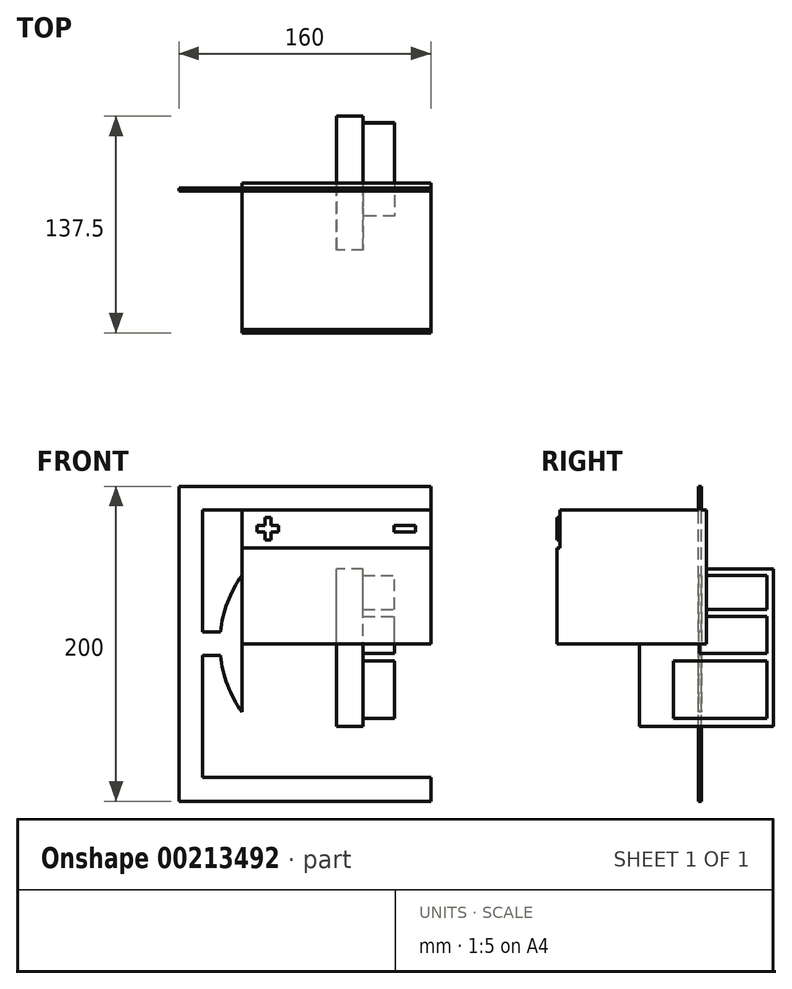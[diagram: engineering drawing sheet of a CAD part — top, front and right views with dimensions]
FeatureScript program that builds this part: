
annotation { "Feature Type Name" : "Feature", "Feature Type Description" : "" }
export const myFeature = defineFeature(function(context is Context, id is Id, definition is map)
    precondition{}
    {
        {
            var Q0;
            Q0=qCreatedBy(makeId("Front.planeOp"),FACE);
            var sketch = newSketch(context, id + "F0", { "sketchPlane" : qUnion([Q0])});
            skCircle(sketch, "E0", {"center": v(0, 0) * mm, "radius": 10 * mm});
            skSolve(sketch);
        }
        {
            var Q0;
            Q0 = qSketchRegion(id + "F0", true);
            extrude(context, id + "F1", {"entities" : qUnion([Q0]), "depth" : 3 * mm});
        }
        {
            var Q0;
            Q0=makeQuery(id+"F1.opExtrude","CAP_FACE",FACE,{"disambiguationData":[OSD([sQuery(id+"F0.wireOp",EDGE,"E0")])],"isStart":false});
            var sketch = newSketch(context, id + "F2", { "sketchPlane" : qUnion([Q0])});
            skCircle(sketch, "E1", {"center": v(0, 0) * mm, "radius": 15 * mm});
            skSolve(sketch);
        }
        {
            var Q0;
            Q0 = qSketchRegion(id + "F2", true);
            extrude(context, id + "F3", {"entities" : qUnion([Q0]), "operationType" : NewBodyOperationType.ADD, "depth" : 1 * mm});
        }
        {
            var Q0;
            Q0=makeQuery(id+"F3.opExtrude","CAP_FACE",FACE,{"disambiguationData":[OSD([sQuery(id+"F2.wireOp",EDGE,"E1")])],"isStart":false});
            var sketch = newSketch(context, id + "F4", { "sketchPlane" : qUnion([Q0])});
            skCircle(sketch, "E2", {"center": v(0, 0) * mm, "radius": 6 * mm});
            skSolve(sketch);
        }
        {
            var Q0;
            Q0 = qSketchRegion(id + "F4", true);
            extrude(context, id + "F5", {"entities" : qUnion([Q0]), "operationType" : NewBodyOperationType.REMOVE, "endBound" : BoundingType.THROUGH_ALL, "oppositeDirection" : true, "depth" : 25 * mm});
        }
        {
            var Q0;
            Q0=makeQuery(id+"F3.opExtrude","CAP_FACE",FACE,{"disambiguationData":[OSD([sQuery(id+"F2.wireOp",EDGE,"E1")])],"isStart":false});
            var sketch = newSketch(context, id + "F6", { "sketchPlane" : qUnion([Q0])});
            skCircle(sketch, "E3", {"center": v(0, 0) * mm, "radius": 15 * mm});
            skCircle(sketch, "E4", {"center": v(0, 0) * mm, "radius": 4.75 * mm});
            skSolve(sketch);
        }
        {
            var Q0;
            Q0 = qSketchRegion(id + "F6", true);
            extrude(context, id + "F7", {"entities" : qUnion([Q0]), "operationType" : NewBodyOperationType.ADD, "depth" : 1 * mm});
        }
        {
            var Q0;
            Q0=makeQuery(id+"F1.opExtrude","CAP_EDGE",EDGE,{"disambiguationData":[OSD([sQuery(id+"F0.wireOp",EDGE,"E0")])],"isStart":true});
            chamfer(context, id + "F8", {"entities" : qUnion([Q0]), "width" : 1 * mm, "tangentPropagation" : true});
        }
        {
            var Q0;
            Q0=makeQuery(id+"F7.opExtrude","CAP_FACE",FACE,{"disambiguationData":[OSD([sQuery(id+"F6.wireOp",EDGE,"E3"),sQuery(id+"F6.wireOp",EDGE,"E4")])],"isStart":false});
            var sketch = newSketch(context, id + "F9", { "sketchPlane" : qUnion([Q0])});
            skLineSegment(sketch, "E5.bottom", {"start": v(-7.5, 100) * mm, "end": v(7.5, 100) * mm});
            skLineSegment(sketch, "E5.top", {"start": v(-7.5, -100) * mm, "end": v(7.5, -100) * mm});
            skLineSegment(sketch, "E5.left", {"start": v(-7.5, 85) * mm, "end": v(-7.5, 7.5) * mm});
            skLineSegment(sketch, "E5.right", {"start": v(7.5, 85) * mm, "end": v(7.5, 7.5) * mm});
            skPoint(sketch, "E5.middle", {"position": v(0, 0) * mm});
            skLineSegment(sketch, "E6.bottom", {"start": v(-85, 7.5) * mm, "end": v(-7.5, 7.5) * mm});
            skLineSegment(sketch, "E6.top", {"start": v(-85, -7.5) * mm, "end": v(-7.5, -7.5) * mm});
            skPoint(sketch, "E6.middle", {"position": v(-16.68, 0) * mm});
            skCircle(sketch, "E7", {"center": v(0, 0) * mm, "radius": 6.5 * mm});
            skLineSegment(sketch, "E8.trimOffspring", {"start": v(7.5, -7.5) * mm, "end": v(45, -7.5) * mm});
            skLineSegment(sketch, "E9.trimOffspring", {"start": v(7.5, -7.5) * mm, "end": v(7.5, -85) * mm});
            skLineSegment(sketch, "E10.trimOffspring", {"start": v(7.5, 7.5) * mm, "end": v(45, 7.5) * mm});
            skLineSegment(sketch, "E11.trimOffspring", {"start": v(-7.5, -7.5) * mm, "end": v(-7.5, -85) * mm});
            skLineSegment(sketch, "E12.bottom", {"start": v(-100, -100) * mm, "end": v(-7.5, -100) * mm});
            skLineSegment(sketch, "E12.top", {"start": v(-100, 100) * mm, "end": v(-7.5, 100) * mm});
            skLineSegment(sketch, "E12.left", {"start": v(-100, -100) * mm, "end": v(-100, 100) * mm});
            skLineSegment(sketch, "E12.right", {"start": v(60, -100) * mm, "end": v(60, 100) * mm});
            skLineSegment(sketch, "E13.0", {"start": v(45, -85) * mm, "end": v(45, -7.5) * mm});
            skLineSegment(sketch, "E13.1", {"start": v(-85, -85) * mm, "end": v(-7.5, -85) * mm});
            skLineSegment(sketch, "E13.2", {"start": v(-85, -85) * mm, "end": v(-85, -7.5) * mm});
            skLineSegment(sketch, "E13.3", {"start": v(-85, 85) * mm, "end": v(-7.5, 85) * mm});
            skLineSegment(sketch, "E14.trimOffspring", {"start": v(45, 7.5) * mm, "end": v(45, 85) * mm});
            skLineSegment(sketch, "E15.trimOffspring", {"start": v(7.5, 85) * mm, "end": v(45, 85) * mm});
            skLineSegment(sketch, "E16.trimOffspring", {"start": v(7.5, -85) * mm, "end": v(45, -85) * mm});
            skLineSegment(sketch, "E17.trimOffspring", {"start": v(-85, 7.5) * mm, "end": v(-85, 85) * mm});
            skLineSegment(sketch, "E18.trimOffspring", {"start": v(7.5, -100) * mm, "end": v(60, -100) * mm});
            skLineSegment(sketch, "E19.trimOffspring", {"start": v(7.5, 100) * mm, "end": v(60, 100) * mm});
            skSolve(sketch);
        }
        {
            var Q0;
            Q0 = qSketchRegion(id + "F9", true);
            extrude(context, id + "F10", {"entities" : qUnion([Q0]), "operationType" : NewBodyOperationType.ADD, "oppositeDirection" : true, "depth" : 2 * mm});
        }
        {
            var Q0;
            Q0=makeQuery(id+"F10.boolean.opBoolean","MERGE",FACE,{"derivedFrom":[makeQuery(id+"F7.opExtrude","CAP_FACE",FACE,{"disambiguationData":[OSD([sQuery(id+"F6.wireOp",EDGE,"E3"),sQuery(id+"F6.wireOp",EDGE,"E4")])],"isStart":false}),makeQuery(id+"F10.opExtrude","CAP_FACE",FACE,{"disambiguationData":[OSD([sQuery(id+"F9.wireOp",EDGE,"E5.bottom"),sQuery(id+"F9.wireOp",EDGE,"E5.top"),sQuery(id+"F9.wireOp",EDGE,"E5.left"),sQuery(id+"F9.wireOp",EDGE,"E5.right"),sQuery(id+"F9.wireOp",EDGE,"E6.bottom"),sQuery(id+"F9.wireOp",EDGE,"E6.top"),sQuery(id+"F9.wireOp",EDGE,"E7"),sQuery(id+"F9.wireOp",EDGE,"E8.trimOffspring"),sQuery(id+"F9.wireOp",EDGE,"E9.trimOffspring"),sQuery(id+"F9.wireOp",EDGE,"E10.trimOffspring"),sQuery(id+"F9.wireOp",EDGE,"E11.trimOffspring"),sQuery(id+"F9.wireOp",EDGE,"E12.bottom"),sQuery(id+"F9.wireOp",EDGE,"E12.top"),sQuery(id+"F9.wireOp",EDGE,"E12.left"),sQuery(id+"F9.wireOp",EDGE,"E12.right"),sQuery(id+"F9.wireOp",EDGE,"E13.0"),sQuery(id+"F9.wireOp",EDGE,"E13.1"),sQuery(id+"F9.wireOp",EDGE,"E13.2"),sQuery(id+"F9.wireOp",EDGE,"E13.3"),sQuery(id+"F9.wireOp",EDGE,"E14.trimOffspring"),sQuery(id+"F9.wireOp",EDGE,"E15.trimOffspring"),sQuery(id+"F9.wireOp",EDGE,"E16.trimOffspring"),sQuery(id+"F9.wireOp",EDGE,"E17.trimOffspring"),sQuery(id+"F9.wireOp",EDGE,"E18.trimOffspring"),sQuery(id+"F9.wireOp",EDGE,"E19.trimOffspring")])],"isStart":true})]});
            var sketch = newSketch(context, id + "F11", { "sketchPlane" : qUnion([Q0])});
            skCircle(sketch, "E20", {"center": v(0, 0) * mm, "radius": 55 * mm});
            skArc(sketch, "E21", {"start": v(60, 43.31) * mm, "mid": v(-74, 0) * mm, "end": v(60, -43.31) * mm});
            skLineSegment(sketch, "E22", {"start": v(60, 43.31) * mm, "end": v(60, -43.31) * mm});
            skSolve(sketch);
        }
        {
            var Q0;
            Q0 = qSketchRegion(id + "F11", true);
            extrude(context, id + "F12", {"entities" : qUnion([Q0]), "operationType" : NewBodyOperationType.ADD, "oppositeDirection" : true, "depth" : 2 * mm});
        }
        {
            var Q0;
            Q0=makeQuery(id+"F12.boolean.opBoolean","MERGE",FACE,{"derivedFrom":[makeQuery(id+"F10.boolean.opBoolean","MERGE",FACE,{"derivedFrom":[makeQuery(id+"F7.opExtrude","CAP_FACE",FACE,{"disambiguationData":[OSD([sQuery(id+"F6.wireOp",EDGE,"E3"),sQuery(id+"F6.wireOp",EDGE,"E4")])],"isStart":false}),makeQuery(id+"F10.opExtrude","CAP_FACE",FACE,{"disambiguationData":[OSD([sQuery(id+"F9.wireOp",EDGE,"E5.bottom"),sQuery(id+"F9.wireOp",EDGE,"E5.top"),sQuery(id+"F9.wireOp",EDGE,"E5.left"),sQuery(id+"F9.wireOp",EDGE,"E5.right"),sQuery(id+"F9.wireOp",EDGE,"E6.bottom"),sQuery(id+"F9.wireOp",EDGE,"E6.top"),sQuery(id+"F9.wireOp",EDGE,"E7"),sQuery(id+"F9.wireOp",EDGE,"E8.trimOffspring"),sQuery(id+"F9.wireOp",EDGE,"E9.trimOffspring"),sQuery(id+"F9.wireOp",EDGE,"E10.trimOffspring"),sQuery(id+"F9.wireOp",EDGE,"E11.trimOffspring"),sQuery(id+"F9.wireOp",EDGE,"E12.bottom"),sQuery(id+"F9.wireOp",EDGE,"E12.top"),sQuery(id+"F9.wireOp",EDGE,"E12.left"),sQuery(id+"F9.wireOp",EDGE,"E12.right"),sQuery(id+"F9.wireOp",EDGE,"E13.0"),sQuery(id+"F9.wireOp",EDGE,"E13.1"),sQuery(id+"F9.wireOp",EDGE,"E13.2"),sQuery(id+"F9.wireOp",EDGE,"E13.3"),sQuery(id+"F9.wireOp",EDGE,"E14.trimOffspring"),sQuery(id+"F9.wireOp",EDGE,"E15.trimOffspring"),sQuery(id+"F9.wireOp",EDGE,"E16.trimOffspring"),sQuery(id+"F9.wireOp",EDGE,"E17.trimOffspring"),sQuery(id+"F9.wireOp",EDGE,"E18.trimOffspring"),sQuery(id+"F9.wireOp",EDGE,"E19.trimOffspring")])],"isStart":true})]}),makeQuery(id+"F12.opExtrude","CAP_FACE",FACE,{"disambiguationData":[OSD([sQuery(id+"F11.wireOp",EDGE,"E20"),sQuery(id+"F11.wireOp",EDGE,"E21"),sQuery(id+"F11.wireOp",EDGE,"E22")])],"isStart":true})]});
            var sketch = newSketch(context, id + "F13", { "sketchPlane" : qUnion([Q0])});
            skLineSegment(sketch, "E23", {"start": v(0, 0) * mm, "end": v(32.2, -50.62) * mm, "construction": true});
            skLineSegment(sketch, "E24", {"start": v(32.2, -50.62) * mm, "end": v(13.65, -62.43) * mm, "construction": true});
            skPoint(sketch, "E25.MirrorP", {"position": v(50.77, -38.81) * mm});
            skCircle(sketch, "E26", {"center": v(0, 0) * mm, "radius": 36.29 * mm, "construction": true});
            skPoint(sketch, "E27.1.0", {"position": v(-47.84, -52.18) * mm});
            skPoint(sketch, "E27.1.1", {"position": v(-9.28, -73.36) * mm});
            skPoint(sketch, "E27.2.0", {"position": v(-68.43, 6.67) * mm});
            skPoint(sketch, "E27.2.1", {"position": v(-68.46, -37.33) * mm});
            skPoint(sketch, "E27.3.0", {"position": v(-26.74, 53.02) * mm});
            skPoint(sketch, "E27.3.1", {"position": v(-65.33, 31.88) * mm});
            skPoint(sketch, "E27.4.0", {"position": v(33.95, 38.76) * mm});
            skPoint(sketch, "E27.4.1", {"position": v(-3.15, 62.43) * mm});
            skPoint(sketch, "E27.center", {"position": v(-8.44, -5.37) * mm});
            skLineSegment(sketch, "E27.anchor1", {"start": v(-8.44, -5.37) * mm, "end": v(13.65, -62.43) * mm, "construction": true});
            skLineSegment(sketch, "E27.anchor2", {"start": v(-8.44, -5.37) * mm, "end": v(33.95, 38.76) * mm, "construction": true});
            skCircle(sketch, "E28", {"center": v(13.65, -62.43) * mm, "radius": 3.18 * mm});
            skCircle(sketch, "E29.MirrorC", {"center": v(50.77, -38.81) * mm, "radius": 3.18 * mm});
            skSolve(sketch);
        }
        {
            var Q0;
            Q0 = qSketchRegion(id + "F13", true);
            extrude(context, id + "F14", {"entities" : qUnion([Q0]), "operationType" : NewBodyOperationType.ADD, "depth" : 8 * mm});
        }
        {
            var Q0;
            Q0=qCreatedBy(makeId("Front.planeOp"),FACE);
            var sketch = newSketch(context, id + "F15", { "sketchPlane" : qUnion([Q0])});
            skLineSegment(sketch, "E30.bottom", {"start": v(60, -85) * mm, "end": v(-60, -85) * mm});
            skLineSegment(sketch, "E30.top", {"start": v(60, 85) * mm, "end": v(-60, 85) * mm});
            skLineSegment(sketch, "E30.left", {"start": v(60, -85) * mm, "end": v(60, 85) * mm});
            skLineSegment(sketch, "E30.right", {"start": v(-60, -85) * mm, "end": v(-60, 85) * mm});
            skPoint(sketch, "E30.middle", {"position": v(0, 0) * mm});
            skSolve(sketch);
        }
        {
            var Q0;
            Q0 = qSketchRegion(id + "F15", true);
            extrude(context, id + "F16", {"entities" : qUnion([Q0]), "depth" : 95 * mm});
        }
        {
            var Q0;
            Q0=makeQuery(id+"F16.opExtrude","CAP_FACE",FACE,{"disambiguationData":[OSD([sQuery(id+"F15.wireOp",EDGE,"E30.bottom"),sQuery(id+"F15.wireOp",EDGE,"E30.top"),sQuery(id+"F15.wireOp",EDGE,"E30.left"),sQuery(id+"F15.wireOp",EDGE,"E30.right")])],"isStart":false});
            var sketch = newSketch(context, id + "F17", { "sketchPlane" : qUnion([Q0])});
            skLineSegment(sketch, "E31.bottom", {"start": v(-60, 85) * mm, "end": v(60, 85) * mm});
            skLineSegment(sketch, "E31.top", {"start": v(-60, 60.98) * mm, "end": v(60, 60.98) * mm});
            skLineSegment(sketch, "E31.left", {"start": v(-60, 85) * mm, "end": v(-60, 60.98) * mm});
            skLineSegment(sketch, "E31.right", {"start": v(60, 85) * mm, "end": v(60, 60.98) * mm});
            skLineSegment(sketch, "E32.bottom", {"start": v(-50.27, 75) * mm, "end": v(-45.38, 75) * mm});
            skLineSegment(sketch, "E32.top", {"start": v(-50.27, 71.06) * mm, "end": v(-45.38, 71.06) * mm});
            skLineSegment(sketch, "E32.left", {"start": v(-50.27, 75) * mm, "end": v(-50.27, 71.06) * mm});
            skLineSegment(sketch, "E32.right", {"start": v(-36.73, 75) * mm, "end": v(-36.73, 71.06) * mm});
            skLineSegment(sketch, "E33", {"start": v(0, 71.7) * mm, "end": v(0, 43.69) * mm, "construction": true});
            skLineSegment(sketch, "E34.MirrorCS", {"start": v(50.27, 75) * mm, "end": v(36.73, 75) * mm});
            skLineSegment(sketch, "E35.MirrorCS", {"start": v(50.27, 71.06) * mm, "end": v(36.73, 71.06) * mm});
            skLineSegment(sketch, "E36.MirrorCS", {"start": v(50.27, 75) * mm, "end": v(50.27, 71.06) * mm});
            skLineSegment(sketch, "E37.MirrorCS", {"start": v(36.73, 75) * mm, "end": v(36.73, 71.06) * mm});
            skLineSegment(sketch, "E38.bottom", {"start": v(-41.62, 65.91) * mm, "end": v(-45.38, 65.91) * mm});
            skLineSegment(sketch, "E38.top", {"start": v(-41.62, 80.16) * mm, "end": v(-45.38, 80.16) * mm});
            skLineSegment(sketch, "E38.left", {"start": v(-41.62, 65.91) * mm, "end": v(-41.62, 71.06) * mm});
            skLineSegment(sketch, "E38.right", {"start": v(-45.38, 65.91) * mm, "end": v(-45.38, 71.06) * mm});
            skPoint(sketch, "E38.middle", {"position": v(-43.5, 73.03) * mm});
            skPoint(sketch, "E38.middle.positionSnap0", {"position": v(-43.5, 75) * mm});
            skPoint(sketch, "E38.middle.positionSnap1", {"position": v(-50.27, 73.03) * mm});
            skPoint(sketch, "E38.centerSnap0", {"position": v(-43.5, 75) * mm});
            skPoint(sketch, "E38.centerSnap1", {"position": v(-50.27, 73.03) * mm});
            skLineSegment(sketch, "E39.trimOffspring", {"start": v(-41.62, 71.06) * mm, "end": v(-36.73, 71.06) * mm});
            skLineSegment(sketch, "E40.trimOffspring", {"start": v(-45.38, 75) * mm, "end": v(-45.38, 80.16) * mm});
            skLineSegment(sketch, "E41.trimOffspring", {"start": v(-41.62, 75) * mm, "end": v(-41.62, 80.16) * mm});
            skLineSegment(sketch, "E42.trimOffspring", {"start": v(-41.62, 75) * mm, "end": v(-36.73, 75) * mm});
            skSolve(sketch);
        }
        {
            var Q0;
            Q0 = qSketchRegion(id + "F17", true);
            extrude(context, id + "F18", {"entities" : qUnion([Q0]), "operationType" : NewBodyOperationType.REMOVE, "oppositeDirection" : true, "depth" : 2 * mm});
        }
        {
            var Q0;
            Q0=makeQuery(id+"F16.opExtrude","SWEPT_BODY",BODY,{"disambiguationData":[OSD([sQuery(id+"F15.wireOp",EDGE,"E30.bottom"),sQuery(id+"F15.wireOp",EDGE,"E30.top"),sQuery(id+"F15.wireOp",EDGE,"E30.left"),sQuery(id+"F15.wireOp",EDGE,"E30.right")])]});
            transform(context, id + "F19", {"entities" : qUnion([Q0]), "transformType" : TransformType.TRANSLATION_3D, "dx" : 0 * mm, "dy" : 0 * mm, "dz" : 0 * mm, "makeCopy" : true});
        }
        {
            var Q0;
            {var subQ0=sQuery(id+"F15.wireOp",EDGE,"E30.bottom");var subQ1=sQuery(id+"F15.wireOp",EDGE,"E30.left");var subQ2=sQuery(id+"F15.wireOp",EDGE,"E30.right");Q0=makeQuery(id+"F19.opPattern","COPY",FACE,{"derivedFrom":makeQuery(id+"F18.boolean.opBoolean","SPLIT",FACE,{"disambiguationData":[TD([makeQuery(id+"F16.opExtrude","SWEPT_FACE",FACE,{"disambiguationData":[OSD([subQ0])]})])],"derivedFrom":makeQuery(id+"F16.opExtrude","CAP_FACE",FACE,{"disambiguationData":[OSD([subQ0,sQuery(id+"F15.wireOp",EDGE,"E30.top"),subQ1,subQ2])],"isStart":false})}),"instanceName":"1"});}
            var sketch = newSketch(context, id + "F20", { "sketchPlane" : qUnion([Q0])});
            skLineSegment(sketch, "E43.bottom", {"start": v(-60, -85) * mm, "end": v(60, -85) * mm});
            skLineSegment(sketch, "E43.top", {"start": v(-60, 0) * mm, "end": v(60, 0) * mm});
            skLineSegment(sketch, "E43.left", {"start": v(-60, -85) * mm, "end": v(-60, 0) * mm});
            skLineSegment(sketch, "E43.right", {"start": v(60, -85) * mm, "end": v(60, 0) * mm});
            skSolve(sketch);
        }
        {
            var Q0;
            Q0 = qSketchRegion(id + "F20", true);
            extrude(context, id + "F21", {"entities" : qUnion([Q0]), "operationType" : NewBodyOperationType.REMOVE, "endBound" : BoundingType.THROUGH_ALL, "oppositeDirection" : true, "depth" : 25 * mm});
        }
        {
            var Q0;
            Q0=qCreatedBy(makeId("Right.planeOp"),FACE);
            var sketch = newSketch(context, id + "F22", { "sketchPlane" : qUnion([Q0])});
            skLineSegment(sketch, "E44.bottom", {"start": v(-42.5, -52.65) * mm, "end": v(42.5, -52.65) * mm});
            skLineSegment(sketch, "E44.top", {"start": v(-42.5, 47.35) * mm, "end": v(42.5, 47.35) * mm});
            skLineSegment(sketch, "E44.left", {"start": v(-42.5, -52.65) * mm, "end": v(-42.5, 47.35) * mm});
            skLineSegment(sketch, "E44.right", {"start": v(42.5, -52.65) * mm, "end": v(42.5, 47.35) * mm});
            skPoint(sketch, "E44.middle", {"position": v(0, -2.65) * mm});
            skSolve(sketch);
        }
        {
            var Q0;
            Q0 = qSketchRegion(id + "F22", true);
            extrude(context, id + "F23", {"entities" : qUnion([Q0]), "depth" : 17 * mm});
        }
        {
            var Q0;
            Q0=makeQuery(id+"F23.opExtrude","CAP_FACE",FACE,{"disambiguationData":[OSD([sQuery(id+"F22.wireOp",EDGE,"E44.bottom"),sQuery(id+"F22.wireOp",EDGE,"E44.top"),sQuery(id+"F22.wireOp",EDGE,"E44.left"),sQuery(id+"F22.wireOp",EDGE,"E44.right")])],"isStart":false});
            var sketch = newSketch(context, id + "F24", { "sketchPlane" : qUnion([Q0])});
            skLineSegment(sketch, "E45.bottom", {"start": v(38.56, -47.53) * mm, "end": v(-20.76, -47.53) * mm});
            skLineSegment(sketch, "E45.top", {"start": v(38.56, -11.05) * mm, "end": v(-20.76, -11.05) * mm});
            skLineSegment(sketch, "E45.left", {"start": v(38.56, -47.53) * mm, "end": v(38.56, -11.05) * mm});
            skLineSegment(sketch, "E45.right", {"start": v(-20.76, -47.53) * mm, "end": v(-20.76, -11.05) * mm});
            skPoint(sketch, "E45.middle", {"position": v(8.9, -29.29) * mm});
            skLineSegment(sketch, "E46.bottom", {"start": v(38.5, -6.3) * mm, "end": v(-4.32, -6.3) * mm});
            skLineSegment(sketch, "E46.top", {"start": v(38.5, 17.39) * mm, "end": v(-4.32, 17.39) * mm});
            skLineSegment(sketch, "E46.left", {"start": v(38.5, -6.3) * mm, "end": v(38.5, 17.39) * mm});
            skLineSegment(sketch, "E46.right", {"start": v(-4.32, -6.3) * mm, "end": v(-4.32, 17.39) * mm});
            skPoint(sketch, "E46.middle", {"position": v(17.1, 5.54) * mm});
            skLineSegment(sketch, "E47.bottom", {"start": v(38.3, 21.92) * mm, "end": v(-2.33, 21.92) * mm});
            skLineSegment(sketch, "E47.top", {"start": v(38.3, 43.46) * mm, "end": v(-2.33, 43.46) * mm});
            skLineSegment(sketch, "E47.left", {"start": v(38.3, 21.92) * mm, "end": v(38.3, 43.46) * mm});
            skLineSegment(sketch, "E47.right", {"start": v(-2.33, 21.92) * mm, "end": v(-2.33, 43.46) * mm});
            skPoint(sketch, "E47.middle", {"position": v(17.99, 32.69) * mm});
            skSolve(sketch);
        }
        {
            var Q0;
            Q0 = qSketchRegion(id + "F24", true);
            extrude(context, id + "F25", {"entities" : qUnion([Q0]), "operationType" : NewBodyOperationType.ADD, "depth" : 20 * mm});
        }
    });
